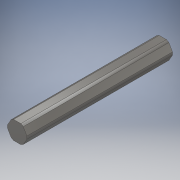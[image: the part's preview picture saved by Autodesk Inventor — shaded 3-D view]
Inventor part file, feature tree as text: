
AUTODESK INVENTOR PART (.ipt)
format: ipt  version: 2019.3 (Build 233278000, 278)  size: 115,200 bytes
history: native  units: in
note: dims shown in document units (in); Inventor stores cm internally (conversion verified against a paired STEP export)
features: extrude x1, sketch x1
ambient origin geometry x8: Origin, YZ Plane, XZ Plane, XY Plane, X Axis, Y Axis, Z Axis, Center Point
bodies: Solid1 (feature_tree)
feature tree (2):
  extrude  "Extrusion1"  Depth=3.0in
  sketch  "Sketch1"  dims[d0=0.375in d1=0.4035in d2=3.0in d3=0.0in]
